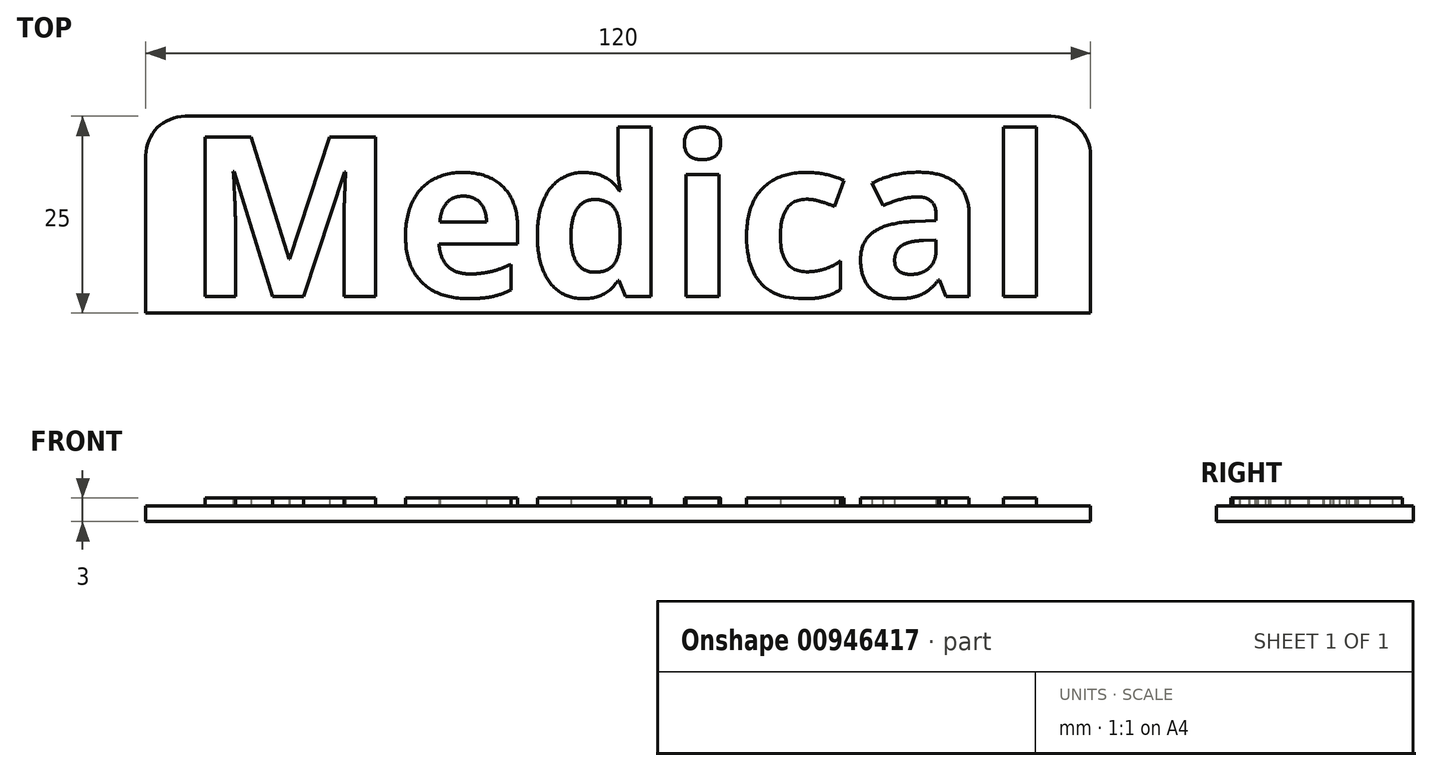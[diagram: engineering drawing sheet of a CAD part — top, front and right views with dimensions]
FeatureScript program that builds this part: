
annotation { "Feature Type Name" : "Feature", "Feature Type Description" : "" }
export const myFeature = defineFeature(function(context is Context, id is Id, definition is map)
    precondition{}
    {
        {
            var Q0;
            Q0=qCreatedBy(makeId("Top.planeOp"),FACE);
            var sketch = newSketch(context, id + "F0", { "sketchPlane" : qUnion([Q0])});
            skLineSegment(sketch, "E0.bottom", {"start": v(-60, 12.5) * mm, "end": v(60, 12.5) * mm});
            skLineSegment(sketch, "E0.top", {"start": v(-60, -12.5) * mm, "end": v(60, -12.5) * mm});
            skLineSegment(sketch, "E0.left", {"start": v(-60, 12.5) * mm, "end": v(-60, -12.5) * mm});
            skLineSegment(sketch, "E0.right", {"start": v(60, 12.5) * mm, "end": v(60, -12.5) * mm});
            skPoint(sketch, "E0.middle", {"position": v(0, 0) * mm});
            skSolve(sketch);
        }
        {
            var Q0;
            Q0=qSketchRegion(id+"F0",true);
            extrude(context, id + "F1", {"entities" : qUnion([Q0]), "depth" : 2 * mm, "offsetDistance" : 25 * mm});
        }
        {
            var Q0;
            Q0=makeQuery(id+"F1.opExtrude","CAP_FACE",FACE,{"disambiguationData":[OSD([sQuery(id+"F0.wireOp",EDGE,"E0.bottom"),sQuery(id+"F0.wireOp",EDGE,"E0.top"),sQuery(id+"F0.wireOp",EDGE,"E0.left"),sQuery(id+"F0.wireOp",EDGE,"E0.right")])],"isStart":false});
            var sketch = newSketch(context, id + "F2", { "sketchPlane" : qUnion([Q0])});
            skText(sketch, "E1", { "text": "Medical\n", "fontName": "OpenSans-Bold.ttf"});
            const initialGuessF2  = {"E1": [-0.055, -0.0104, 1, 0, 0.0204]};
            skSetInitialGuess(sketch, initialGuessF2);
            skSolve(sketch);
        }
        {
            var Q0;
            Q0=qSketchRegion(id+"F2",true);
            extrude(context, id + "F3", {"entities" : qUnion([Q0]), "operationType" : NewBodyOperationType.ADD, "depth" : 1 * mm, "offsetDistance" : 25 * mm});
        }
        {
            var Q0;
            Q0=makeQuery(id+"F1.opExtrude","SWEPT_EDGE",EDGE,{"disambiguationData":[OSD([sQuery(id+"F0.wireOp",EDGE,"E0.bottom"),sQuery(id+"F0.wireOp",EDGE,"E0.left")])]});
            var Q1;
            Q1=makeQuery(id+"F1.opExtrude","SWEPT_EDGE",EDGE,{"disambiguationData":[OSD([sQuery(id+"F0.wireOp",EDGE,"E0.bottom"),sQuery(id+"F0.wireOp",EDGE,"E0.right")])]});
            fillet(context, id + "F4", {"entities" : qUnion([Q0, Q1]), "radius" : 5 * mm, "tangentPropagation" : true, "allowEdgeOverflow" : false});
        }
    });
